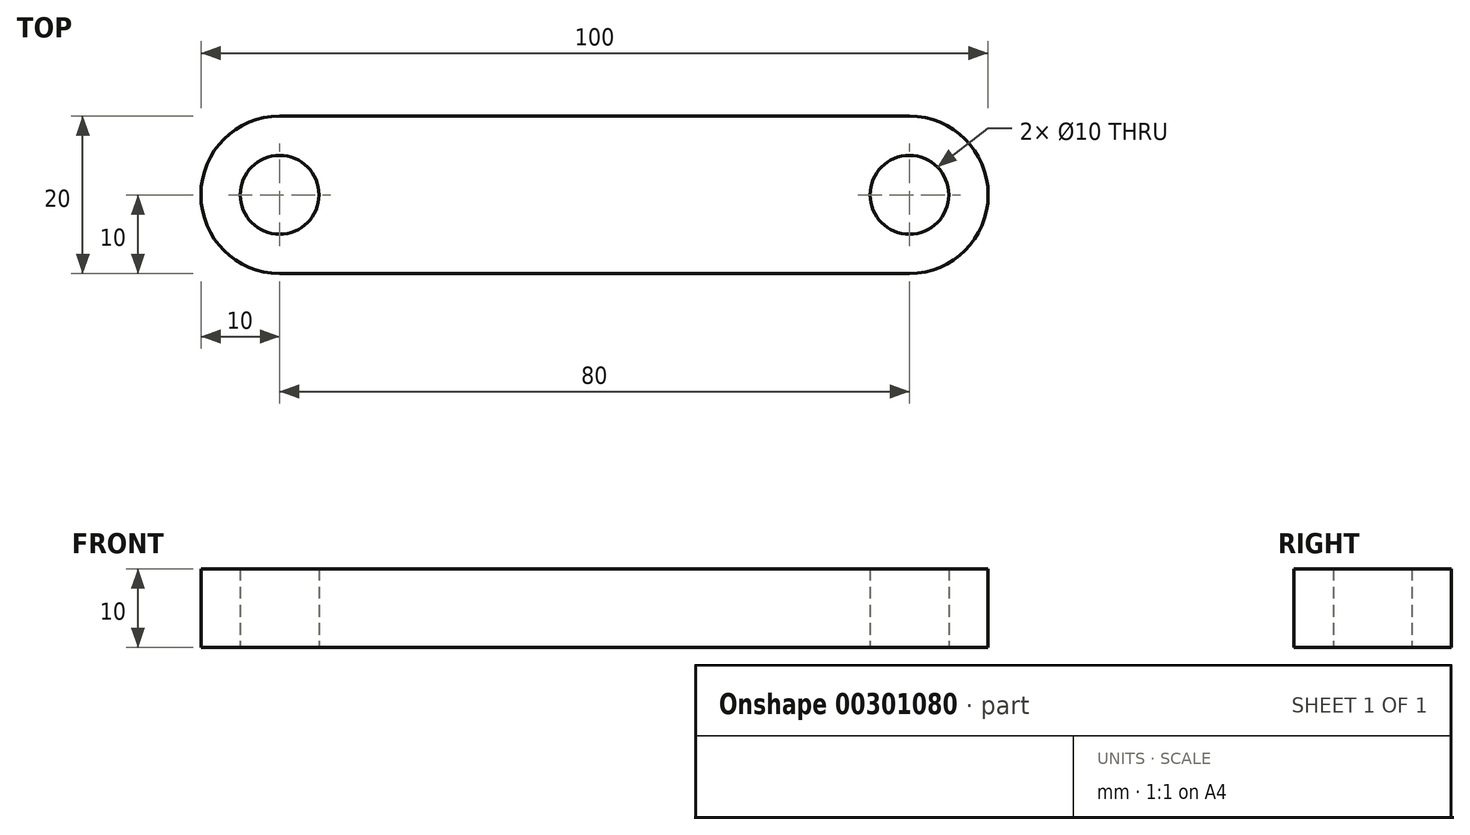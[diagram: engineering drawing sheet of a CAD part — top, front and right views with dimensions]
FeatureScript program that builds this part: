
annotation { "Feature Type Name" : "Feature", "Feature Type Description" : "" }
export const myFeature = defineFeature(function(context is Context, id is Id, definition is map)
    precondition{}
    {
        {
            var Q0;
            Q0=qCreatedBy(makeId("Top.planeOp"),FACE);
            var sketch = newSketch(context, id + "F0", { "sketchPlane" : qUnion([Q0])});
            skLineSegment(sketch, "E0", {"start": v(0, 20) * mm, "end": v(80, 20) * mm});
            skLineSegment(sketch, "E1", {"start": v(0, 0) * mm, "end": v(80, 0) * mm});
            skArc(sketch, "E2", {"start": v(0, 20) * mm, "mid": v(-10, 10) * mm, "end": v(0, 0) * mm});
            skArc(sketch, "E3", {"start": v(80, 0) * mm, "mid": v(90, 10) * mm, "end": v(80, 20) * mm});
            skCircle(sketch, "E4", {"center": v(0, 10) * mm, "radius": 5 * mm});
            skCircle(sketch, "E5", {"center": v(80, 10) * mm, "radius": 5 * mm});
            skSolve(sketch);
        }
        {
            var Q0;
            Q0 = qSketchRegion(id + "F0", true);
            extrude(context, id + "F1", {"entities" : qUnion([Q0]), "depth" : 10 * mm});
        }
    });
